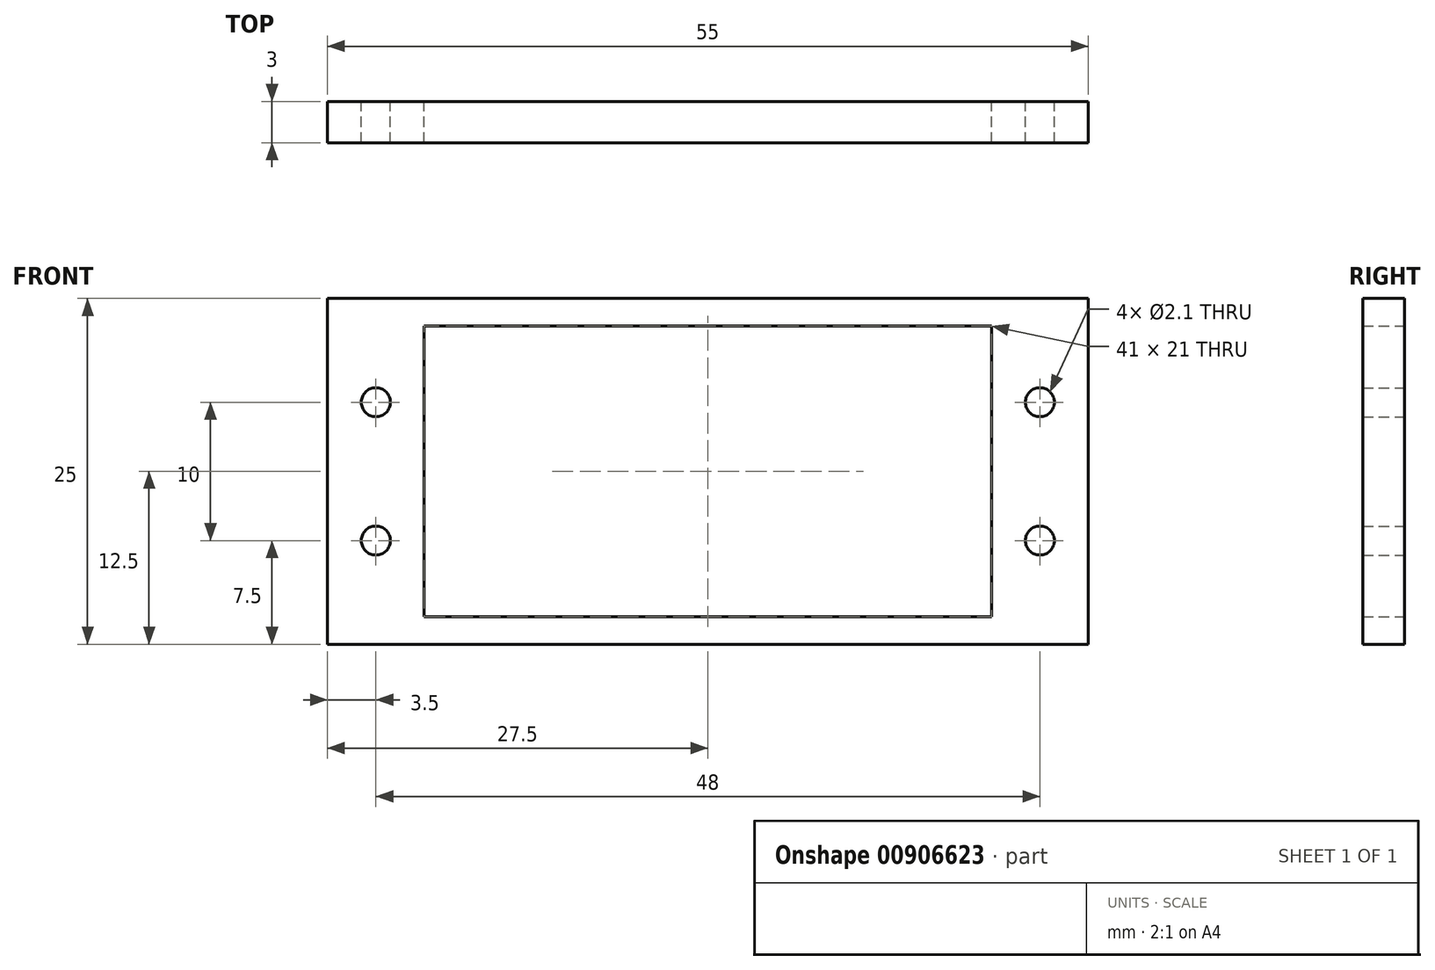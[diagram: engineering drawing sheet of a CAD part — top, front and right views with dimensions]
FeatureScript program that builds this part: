
annotation { "Feature Type Name" : "Feature", "Feature Type Description" : "" }
export const myFeature = defineFeature(function(context is Context, id is Id, definition is map)
    precondition{}
    {
        {
            var Q0;
            Q0=qCreatedBy(makeId("Front.planeOp"),FACE);
            var sketch = newSketch(context, id + "F0", { "sketchPlane" : qUnion([Q0])});
            skLineSegment(sketch, "E0.bottom", {"start": v(0, 0) * mm, "end": v(-41, 0) * mm});
            skLineSegment(sketch, "E0.top", {"start": v(0, 21) * mm, "end": v(-41, 21) * mm});
            skLineSegment(sketch, "E0.left", {"start": v(0, 0) * mm, "end": v(0, 5.5) * mm});
            skLineSegment(sketch, "E0.right", {"start": v(-41, 0) * mm, "end": v(-41, 5.5) * mm});
            skLineSegment(sketch, "E1.bottom", {"start": v(3.5, 5.5) * mm, "end": v(0, 5.5) * mm});
            skLineSegment(sketch, "E1.top", {"start": v(3.5, 15.5) * mm, "end": v(0, 15.5) * mm});
            skLineSegment(sketch, "E1.left", {"start": v(3.5, 5.5) * mm, "end": v(3.5, 15.5) * mm});
            skLineSegment(sketch, "E1.right", {"start": v(-44.5, 5.5) * mm, "end": v(-44.5, 15.5) * mm});
            skLineSegment(sketch, "E2.trimOffspring", {"start": v(-41, 15.5) * mm, "end": v(-41, 21) * mm});
            skLineSegment(sketch, "E3.trimOffspring", {"start": v(0, 15.5) * mm, "end": v(0, 21) * mm});
            skLineSegment(sketch, "E4.trimOffspring", {"start": v(-41, 5.5) * mm, "end": v(-44.5, 5.5) * mm});
            skLineSegment(sketch, "E5.trimOffspring", {"start": v(-41, 15.5) * mm, "end": v(-44.5, 15.5) * mm});
            skCircle(sketch, "E6", {"center": v(-44.5, 15.5) * mm, "radius": 1.05 * mm});
            skCircle(sketch, "E7", {"center": v(-44.5, 5.5) * mm, "radius": 1.05 * mm});
            skCircle(sketch, "E8", {"center": v(3.5, 5.5) * mm, "radius": 1.05 * mm});
            skCircle(sketch, "E9", {"center": v(3.5, 15.5) * mm, "radius": 1.05 * mm});
            skLineSegment(sketch, "E10.bottom", {"start": v(7, -2) * mm, "end": v(-48, -2) * mm});
            skLineSegment(sketch, "E10.top", {"start": v(7, 23) * mm, "end": v(-48, 23) * mm});
            skLineSegment(sketch, "E10.left", {"start": v(7, -2) * mm, "end": v(7, 23) * mm});
            skLineSegment(sketch, "E10.right", {"start": v(-48, -2) * mm, "end": v(-48, 23) * mm});
            skLineSegment(sketch, "E11", {"start": v(-41, 15.5) * mm, "end": v(-41, 5.5) * mm});
            skLineSegment(sketch, "E12", {"start": v(0, 15.5) * mm, "end": v(0, 5.5) * mm});
            skSolve(sketch);
        }
        {
            var Q0;
            {var subQ0=sQuery(id+"F0.wireOp",EDGE,"E11");Q0=makeQuery(id+"F0.imprint","IMPRINT",FACE,{"disambiguationData":[TD([[makeQuery(id+"F0.imprint","IMPRINT",EDGE,{"derivedFrom":subQ0}),-1.0]])]});}
            var Q1;
            {var subQ7=sQuery(id+"F0.wireOp",EDGE,"E12");Q1=makeQuery(id+"F0.imprint","IMPRINT",FACE,{"disambiguationData":[TD([[makeQuery(id+"F0.imprint","IMPRINT",EDGE,{"derivedFrom":subQ7}),1.0]])]});}
            var Q2;
            Q2=makeQuery(id+"F0.imprint","IMPRINT",FACE,{"disambiguationData":[TD([[makeQuery(id+"F0.imprint","IMPRINT",EDGE,{"derivedFrom":sQuery(id+"F0.wireOp",EDGE,"E0.bottom")}),1.0]])]});
            extrude(context, id + "F1", {"entities" : qUnion([Q0, Q1, Q2]), "depth" : 25 * mm, "offsetDistance" : 25 * mm, "hasSecondDirection" : true, "secondDirectionOppositeDirection" : false, "secondDirectionDepth" : 22 * mm});
        }
    });
